# Revit family: QF_BPRO_BPT E 24 N_575197
name_source: partatom
category: Sonderausstattung
revit_build: Autodesk Revit 2018 (Build: 20181015_0930(x64)
units: mm (PartAtom-declared; Revit-internal decimal feet)

## family parameters
Arbeitsebenenbasiert = Nein
Beim Laden mit Abzugskörper schneiden = Nein
Bemaßung runder Anschluss = Durchmesser verwenden
Gemeinsam genutzt = Nein
Immer vertikal = Ja
Raumberechnungspunkt = Nein
Teiletyp = Normal

## types (1)
- BPT E 24 N
    Accessory = Ja
    Beschreibung = BPT E 24 neutral
B.PROTHERM E food transport container
made of stainless steel, mobile, synthetic
castors, corrosion-resistant in compliance with DIN 18867-8, castors 125 mm dia., 2 fixed and 2 steering castors, 2 of which have brakes
    CE Approved = Ja
    Depth Actual = 821 mm  [stored 2.69357 ft]
    Foodservice Equipment Identifier = Ja
    Height Actual = 1302 mm  [stored 4.27165 ft]
    Hersteller = B.PRO GmbH
    Item Number = 575197
    Kosten = 4000 $
    Length Actual = 590 mm  [stored 1.9357 ft]
    Masterspec = Dimensions

Length:				   590 mm
Width:			   821 mm
Height:			 1302 mm


Model

Design
The B.PROTHERM is made of AISI 304 stainless steel. The surface is micro-polished.  
Body and hinged door are double-walled and fitted with CFC-free PUR foam panels. The B.PROTHERM is mobile thanks to synthetic castors (2 fixed and 2 steering castors, 2 of which have brakes, castor diameter 125 mm), corrosion-resistant in compliance with DIN 18867, Part 8. The sturdy, synthetic base structure with integrated all-round bumper rail protects the unit and furniture from damage.

Body
The BPT E 24 N's enclosed top cover features stacking nubs, meaning B.PROTHERM synthetic containers can be stacked on it. The base and rear and side walls are fitted with all-round edge radius R2 and are spot-welded at their points of contact (hygienic type HS). The interior is fully equipped with 24 pairs of deep-drawn stainless steel ledge walls for easy cleaning and maximum hygiene. The support ledges have a uniform spacing of 38.3 mm to hold Gastronorm containers size GN 1/1 or their subdivisions. This means all common spacing dimensions (about 75 mm, 115 mm) can be housed in a single unit and ensures efficient use of the interior. 
Interior and exterior body are vertically connected with synthetic profiles and thermally separated.

The B.PROTHERM is equipped with 4 vertical push handles as standard to ensure optimum handling on all sides. The ergonomic length of the handles makes the trolley easy to manoeuvre for any trolley size. The push handles are located within the bumper rail to prevent the hands from being crushed when rolling through doors and narrow corridors.

 
Door
The trolley is equipped with a door on its front that can be opened 270° and features a lock on its bottom plate. The door is inside the bumper rail when open or closed and is thus protected from damage. The push handles are still accessible when the door is open. The robust door hinges are made of stainless steel investment casting. The hinge design eliminates risk of injury if a user should accidentally take hold of the hinge.
The door is also fitted with an all-round, food-safe seal (TPE) that closes against the trolley body and can be removed. 

The door is fitted with a 2-point locking system. It is easy to open from the outside by simply pushing up the door handle. 
The B.PROTHERM has a push-button which glows in the dark in its interior. The patented panic opening can be identified if someone should get accidentally locked inside the interior and the door lock can be unlocked from the inside by pressing the button. What is known as the afterglow effect meets the requirements for safety-relevant components specified in ISO 16069. 

Options

•	Can be customised with powder coating on body and doors in 12 colours
•	Digitisation/connectivity for digital hygiene, temperature and process management using optionally built-in sensor technology 
•	Additional bumper rail on the top made of solid synthetic 
•	Top with stainless steel railing on 3 sides
•	(Smooth) top with stainless steel railing on 
4 sides
•	Hygienic type H1
•	Door, lockable
•	Convenient door opening, with foot operation
•	Stainless-steel castors, 125 mm in diameter, 
2 fixed and 2 steering castors with brakes 
•	Anti-static castors, 125 mm in diameter, 
2 fixed and 2 steering castors with brakes, 
corrosion-resistant as per DIN 18867-8, synthetic
•	Galvanised steel castors, 160 mm in diameter, 
2 fixed and 2 steering castors with brakes 
•	Galvanised steel castors with elastic tyres, 
160 mm in diameter, 2 fixed and 2 steering castors with brakes 
•	Stainless-steel castors, 160 mm in diameter, 
2 fixed and 2 steering castors with brakes 
•	Stainless-steel castors with elastic tyres, 
160 mm in diameter, 2 fixed and 2 steering castors with brakes 

Accessories

•	Thermal separation element to sub-divide the interior to allow use of different temperature zones. 
•	Eutectic plate -3 °C, synthetic 
(Order no.: 568 136)
•	Eutectic plate -12 °C, synthetic 
(Order no.: 573 332)
•	Slide-in frame to sub-divide GN containers with a max. depth of 150 mm (order no. 564 352)
•	GN support bars for variable insertion of GN containers of the size GN 1/4, GN 1/6, GN 1/9 in the slide-in frame (ST 3 order no. 550 650; ST 5 order no. 550 651)
•	Menu card holder for the door on front, stainless steel, to attach DIN A5 and DIN A6 menu cards (order no. 575 230)
•	Menu card holder for the door on front, stainless steel, to attach DIN A5 and DIN A6 menu cards
•	BPT E menu card, DIN A6 (order no. 564 353) 
•	Special pen for marking BPT E menu cards (order no. 564 361)
•	Menu card box, synthetic (order no. 564 355)

Technical data

Material:	Stainless steel,
	synthetic
Insulating material:		PUR foam panels, CFC-free 
Weight:	65 kg
Capacity:	12 x GN 1/1-65
	24 pairs of deep-drawn support ledges
	Space between ledges of 38.3 mm


 
Special features

•	Extremely efficient, flexible use of interior thanks to uniform space between ledges of 38.3 mm
•	Deep-drawn stainless steel ledge walls for easy cleaning and maximum hygiene.
•	Sturdy, enclosed, solid, synthetic base structure with integrated all-round bumper rail.
•	Hinged door with door opening of 270°, with lock 
•	Optional connectivity function 

Make

Manufacturer:			B.PRO
Model:	BPT E 24 N
	B.PROTHERM
Order no.			575 197
    Material = QF_Metal-Stainless-Steel_general
    Material Rollen = QF_Plastic-Dark_Grey-Matt
    Material Stoßschutz = QF_Plastic-Black-Matt
    Model Warning = Upright transport position
Transport the unit in an upright position only.
Transport with a truck or delivery vehicle
The unit may only be transported in a truck or delivery vehicle which features a loading ramp.
The loading ramp must not exceed an angle of inclination of 10°.
The unit is not properly secured for transport if only the castor brakes have been applied.
Secure the unit on all four sides to prevent it from shifting.
Secure the unit against vertical movement during transport.
Use padded locking bars.

Loading
To prevent extension of the centre of gravity to the unit top, load unit from the bottom up when
loading partially.
Do not exceed the upper weight limit specified in the technical data when loading..

Detailed safety information can be found in the operating instructions.
    Modell = BPT E 24 N
    Typenkommentare = food transport container neutral
    URL = https://www.bpro-solutions.com
    URL Manufacturer = https://www.bpro-solutions.com
    URL Recommended Spares List = https://www.bpro-solutions.com
    Weight = 65.00 kg

note: [stored X ft] marks values corroborated as IEEE doubles in the binary element streams (Revit-internal decimal feet)
